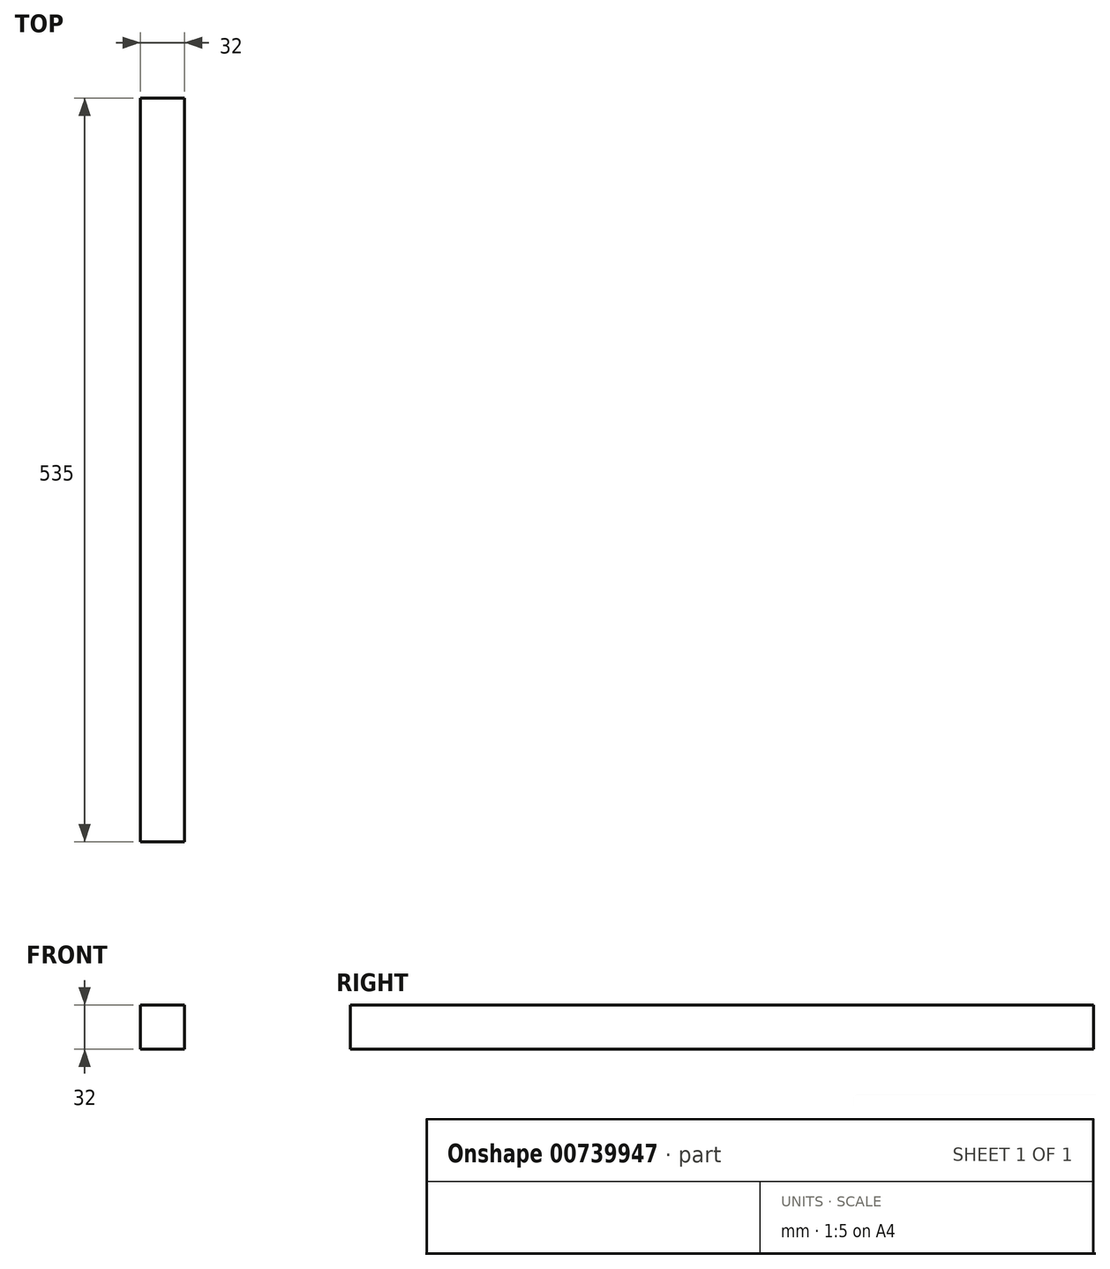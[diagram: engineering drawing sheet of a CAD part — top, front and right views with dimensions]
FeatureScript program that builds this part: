
annotation { "Feature Type Name" : "Feature", "Feature Type Description" : "" }
export const myFeature = defineFeature(function(context is Context, id is Id, definition is map)
    precondition{}
    {
        {
            var Q0;
            Q0=qCreatedBy(makeId("Front.planeOp"),FACE);
            var sketch = newSketch(context, id + "F0", { "sketchPlane" : qUnion([Q0])});
            skLineSegment(sketch, "E0.bottom", {"start": v(16, -16) * mm, "end": v(-16, -16) * mm});
            skLineSegment(sketch, "E0.top", {"start": v(16, 16) * mm, "end": v(-16, 16) * mm});
            skLineSegment(sketch, "E0.left", {"start": v(16, -16) * mm, "end": v(16, 16) * mm});
            skLineSegment(sketch, "E0.right", {"start": v(-16, -16) * mm, "end": v(-16, 16) * mm});
            skPoint(sketch, "E0.middle", {"position": v(0, 0) * mm});
            skSolve(sketch);
        }
        {
            var Q0;
            Q0=makeQuery(id+"F0.imprint","IMPRINT",FACE,{"disambiguationData":[TD([[makeQuery(id+"F0.imprint","IMPRINT",EDGE,{"derivedFrom":sQuery(id+"F0.wireOp",EDGE,"E0.bottom")}),-1.0]])]});
            extrude(context, id + "F1", {"entities" : qUnion([Q0]), "oppositeDirection" : true, "depth" : 535 * mm, "offsetDistance" : 25 * mm, "symmetric" : true});
        }
    });
